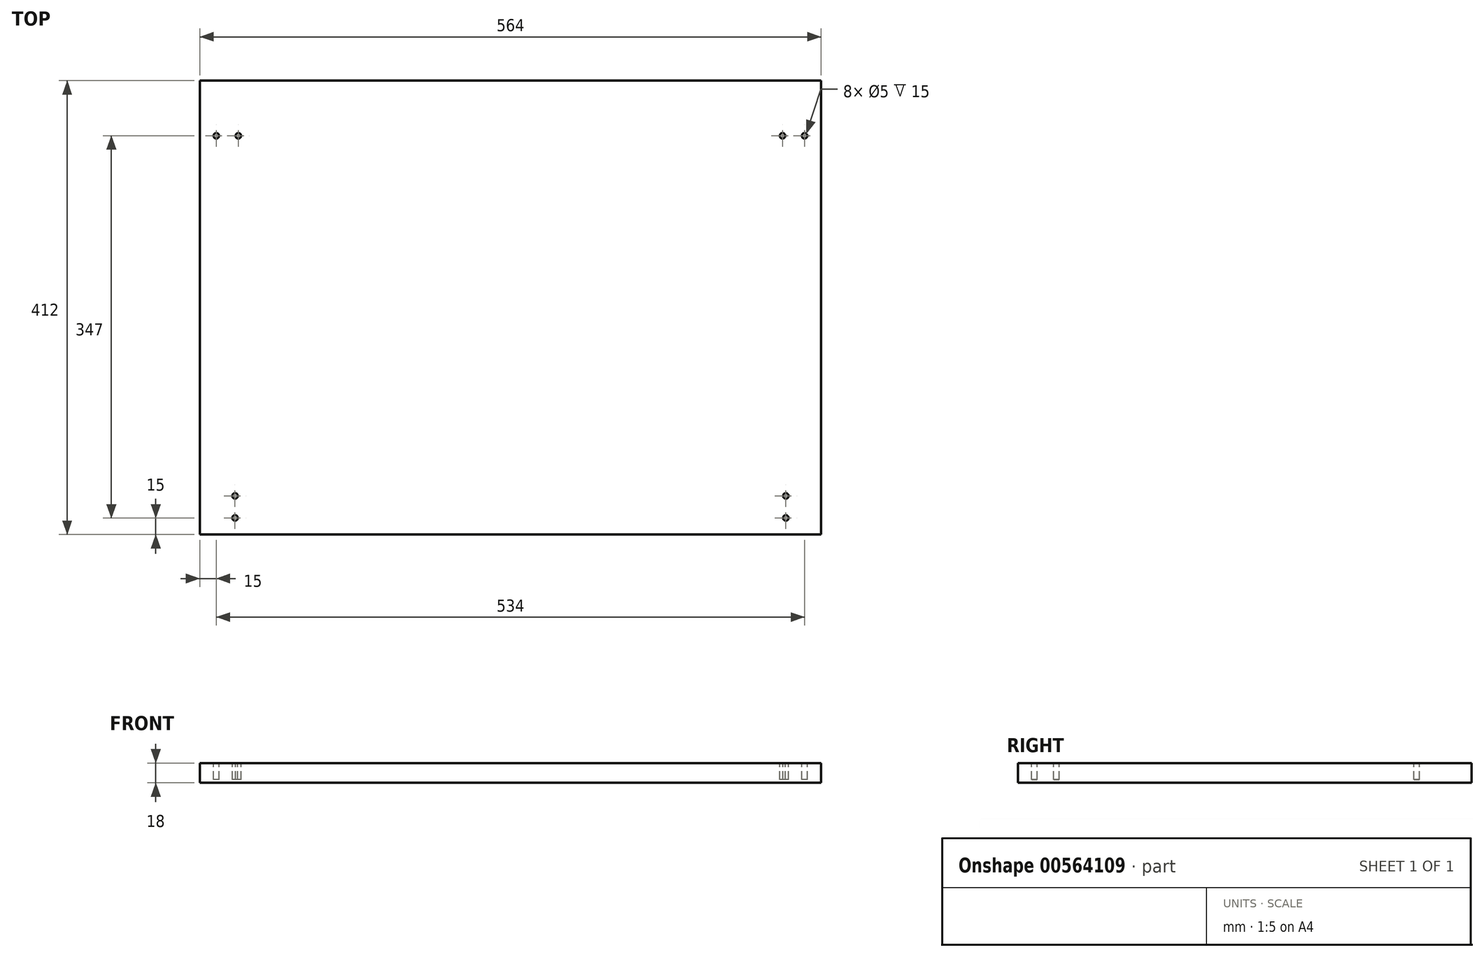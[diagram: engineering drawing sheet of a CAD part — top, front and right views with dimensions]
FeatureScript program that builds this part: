
annotation { "Feature Type Name" : "Feature", "Feature Type Description" : "" }
export const myFeature = defineFeature(function(context is Context, id is Id, definition is map)
    precondition{}
    {
        {
            var Q0;
            Q0=qCreatedBy(makeId("Top.planeOp"),FACE);
            var sketch = newSketch(context, id + "F0", { "sketchPlane" : qUnion([Q0])});
            skLineSegment(sketch, "E0.bottom", {"start": v(-282, 206) * mm, "end": v(282, 206) * mm});
            skLineSegment(sketch, "E0.top", {"start": v(-282, -206) * mm, "end": v(282, -206) * mm});
            skLineSegment(sketch, "E0.left", {"start": v(-282, 206) * mm, "end": v(-282, -206) * mm});
            skLineSegment(sketch, "E0.right", {"start": v(282, 206) * mm, "end": v(282, -206) * mm});
            skSolve(sketch);
        }
        {
            var Q0;
            Q0 = qSketchRegion(id + "F0", true);
            extrude(context, id + "F1", {"entities" : qUnion([Q0]), "depth" : 18 * mm, "offsetDistance" : 25 * mm});
        }
        {
            var Q0;
            Q0=makeQuery(id+"F1.opExtrude","CAP_FACE",FACE,{"disambiguationData":[OSD([sQuery(id+"F0.wireOp",EDGE,"E0.bottom"),sQuery(id+"F0.wireOp",EDGE,"E0.top"),sQuery(id+"F0.wireOp",EDGE,"E0.left"),sQuery(id+"F0.wireOp",EDGE,"E0.right")])],"isStart":false});
            var sketch = newSketch(context, id + "F2", { "sketchPlane" : qUnion([Q0])});
            skCircle(sketch, "E1", {"center": v(-267, 156) * mm, "radius": 2.5 * mm});
            skCircle(sketch, "E2", {"center": v(-247, 156) * mm, "radius": 2.5 * mm});
            skCircle(sketch, "E3", {"center": v(-250, -191) * mm, "radius": 2.5 * mm});
            skCircle(sketch, "E4", {"center": v(-250, -171) * mm, "radius": 2.5 * mm});
            skCircle(sketch, "E5.MirrorC", {"center": v(250, -171) * mm, "radius": 2.5 * mm});
            skCircle(sketch, "E6.MirrorC", {"center": v(250, -191) * mm, "radius": 2.5 * mm});
            skCircle(sketch, "E7.MirrorC", {"center": v(267, 156) * mm, "radius": 2.5 * mm});
            skCircle(sketch, "E8.MirrorC", {"center": v(247, 156) * mm, "radius": 2.5 * mm});
            skSolve(sketch);
        }
        {
            var Q0;
            Q0 = qSketchRegion(id + "F2", true);
            extrude(context, id + "F3", {"entities" : qUnion([Q0]), "operationType" : NewBodyOperationType.REMOVE, "oppositeDirection" : true, "depth" : 15 * mm, "offsetDistance" : 25 * mm});
        }
    });
